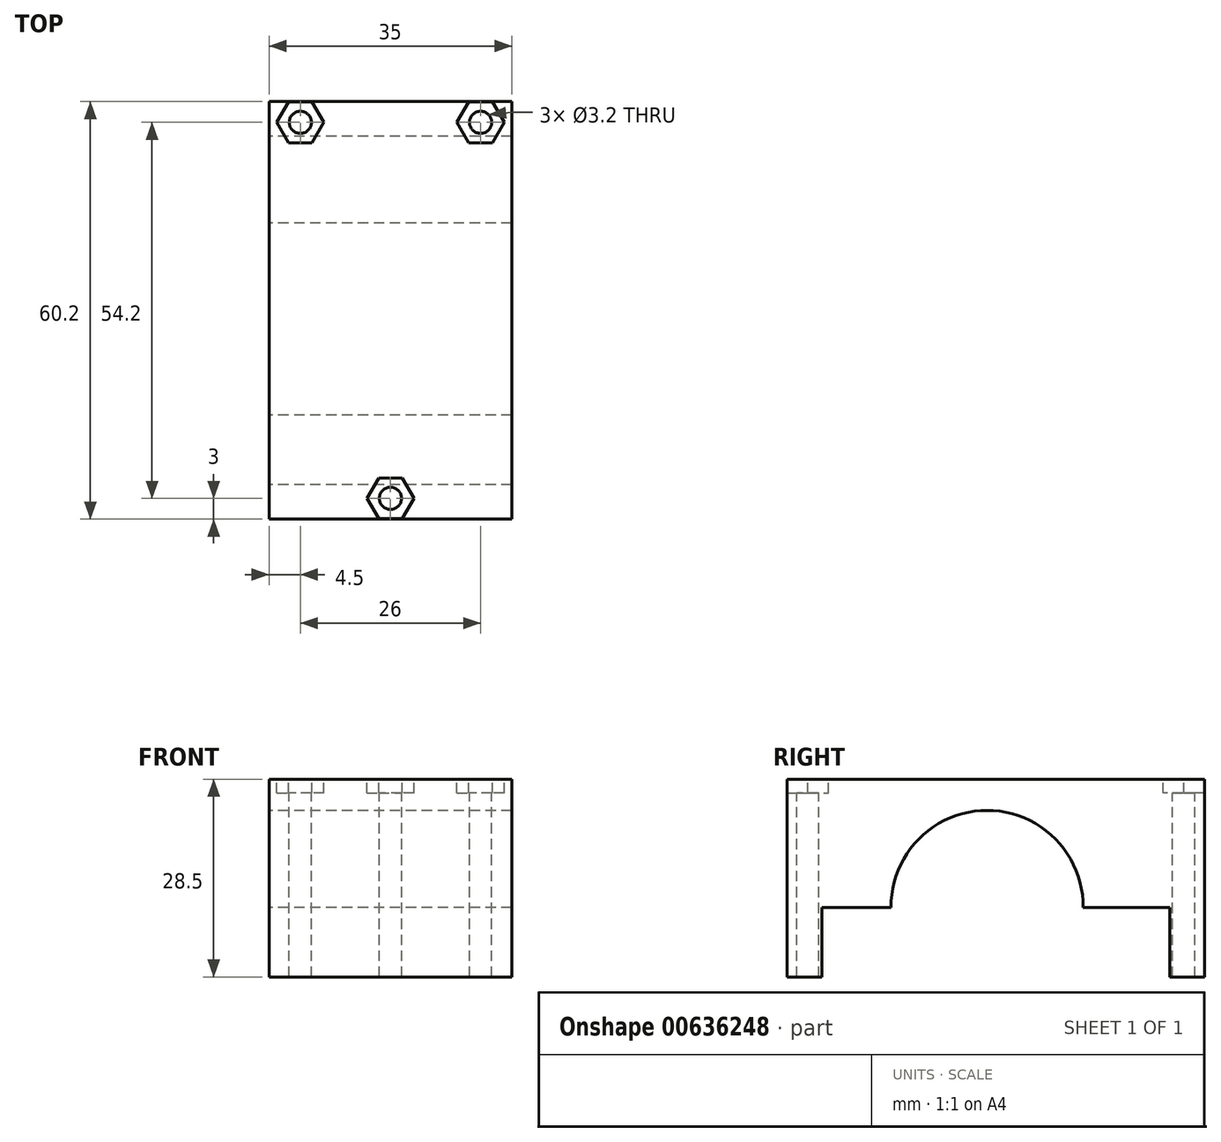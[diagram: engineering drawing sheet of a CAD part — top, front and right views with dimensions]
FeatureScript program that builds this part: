
annotation { "Feature Type Name" : "Feature", "Feature Type Description" : "" }
export const myFeature = defineFeature(function(context is Context, id is Id, definition is map)
    precondition{}
    {
        {
            var Q0;
            Q0=qCreatedBy(makeId("Right.planeOp"),FACE);
            var sketch = newSketch(context, id + "F0", { "sketchPlane" : qUnion([Q0])});
            skLineSegment(sketch, "E0.top", {"start": v(0, 28.5) * mm, "end": v(-60.2, 28.5) * mm});
            skLineSegment(sketch, "E0.left", {"start": v(0, 0) * mm, "end": v(0, 28.5) * mm});
            skLineSegment(sketch, "E0.right", {"start": v(-60.2, 0) * mm, "end": v(-60.2, 28.5) * mm});
            skLineSegment(sketch, "E1", {"start": v(-60.2, 0) * mm, "end": v(-55.2, 0) * mm});
            skLineSegment(sketch, "E2", {"start": v(0, 0) * mm, "end": v(-5, 0) * mm});
            skLineSegment(sketch, "E3", {"start": v(-55.2, 0) * mm, "end": v(-55.2, 10) * mm});
            skLineSegment(sketch, "E4", {"start": v(-5, 0) * mm, "end": v(-5, 10) * mm});
            skLineSegment(sketch, "E5", {"start": v(-55.2, 10) * mm, "end": v(-45.2, 10) * mm});
            skLineSegment(sketch, "E6", {"start": v(-5, 10) * mm, "end": v(-17.5, 10) * mm});
            skArc(sketch, "E7", {"start": v(-17.5, 10) * mm, "mid": v(-31.35, 24) * mm, "end": v(-45.2, 10) * mm});
            skPoint(sketch, "E8", {"position": v(-31.35, 24) * mm});
            skSolve(sketch);
        }
        {
            var Q0;
            Q0 = qSketchRegion(id + "F0", true);
            extrude(context, id + "F1", {"entities" : qUnion([Q0]), "depth" : 35 * mm, "offsetDistance" : 25 * mm});
        }
        {
            var Q0;
            Q0=makeQuery(id+"F1.opExtrude","SWEPT_FACE",FACE,{"disambiguationData":[OSD([sQuery(id+"F0.wireOp",EDGE,"E0.top")])]});
            var sketch = newSketch(context, id + "F2", { "sketchPlane" : qUnion([Q0])});
            skCircle(sketch, "E9", {"center": v(4.5, -3) * mm, "radius": 1.6 * mm});
            skCircle(sketch, "E10", {"center": v(30.5, -3) * mm, "radius": 1.6 * mm});
            skCircle(sketch, "E11", {"center": v(17.5, -57.2) * mm, "radius": 1.6 * mm});
            skSolve(sketch);
        }
        {
            var Q0;
            Q0 = qSketchRegion(id + "F2", true);
            extrude(context, id + "F3", {"entities" : qUnion([Q0]), "operationType" : NewBodyOperationType.REMOVE, "endBound" : BoundingType.UP_TO_NEXT, "oppositeDirection" : true, "depth" : 25 * mm, "offsetDistance" : 25 * mm});
        }
        {
            var Q0;
            Q0=makeQuery(id+"F1.opExtrude","SWEPT_FACE",FACE,{"disambiguationData":[OSD([sQuery(id+"F0.wireOp",EDGE,"E0.top")])]});
            var sketch = newSketch(context, id + "F4", { "sketchPlane" : qUnion([Q0])});
            skCircle(sketch, "E12.cCircle", {"center": v(4.5, -3) * mm, "radius": 2.95 * mm, "construction": true});
            skLineSegment(sketch, "E12.0", {"start": v(6.2, -5.95) * mm, "end": v(2.8, -5.95) * mm});
            skLineSegment(sketch, "E12.1", {"start": v(2.8, -5.95) * mm, "end": v(1.1, -3) * mm});
            skLineSegment(sketch, "E12.2", {"start": v(1.1, -3) * mm, "end": v(2.8, -0.05) * mm});
            skLineSegment(sketch, "E12.3", {"start": v(2.8, -0.05) * mm, "end": v(6.2, -0.05) * mm});
            skLineSegment(sketch, "E12.4", {"start": v(6.2, -0.05) * mm, "end": v(7.9, -3) * mm});
            skLineSegment(sketch, "E12.5", {"start": v(7.9, -3) * mm, "end": v(6.2, -5.95) * mm});
            skPoint(sketch, "E12.0.midPoint", {"position": v(4.5, -5.95) * mm});
            skCircle(sketch, "E13.cCircle", {"center": v(30.5, -3) * mm, "radius": 2.95 * mm, "construction": true});
            skLineSegment(sketch, "E13.0", {"start": v(32.2, -5.95) * mm, "end": v(28.8, -5.95) * mm});
            skLineSegment(sketch, "E13.1", {"start": v(28.8, -5.95) * mm, "end": v(27.1, -3) * mm});
            skLineSegment(sketch, "E13.2", {"start": v(27.1, -3) * mm, "end": v(28.8, -0.05) * mm});
            skLineSegment(sketch, "E13.3", {"start": v(28.8, -0.05) * mm, "end": v(32.2, -0.05) * mm});
            skLineSegment(sketch, "E13.4", {"start": v(32.2, -0.05) * mm, "end": v(33.9, -3) * mm});
            skLineSegment(sketch, "E13.5", {"start": v(33.9, -3) * mm, "end": v(32.2, -5.95) * mm});
            skPoint(sketch, "E13.0.midPoint", {"position": v(30.5, -5.95) * mm});
            skPoint(sketch, "E14.0.midPoint", {"position": v(17.5, -60.15) * mm});
            skCircle(sketch, "E15.cCircle", {"center": v(17.5, -57.2) * mm, "radius": 2.95 * mm, "construction": true});
            skLineSegment(sketch, "E15.0", {"start": v(15.8, -54.25) * mm, "end": v(19.2, -54.25) * mm});
            skLineSegment(sketch, "E15.1", {"start": v(19.2, -54.25) * mm, "end": v(20.9, -57.2) * mm});
            skLineSegment(sketch, "E15.2", {"start": v(20.9, -57.2) * mm, "end": v(19.2, -60.15) * mm});
            skLineSegment(sketch, "E15.3", {"start": v(19.2, -60.15) * mm, "end": v(15.8, -60.15) * mm});
            skLineSegment(sketch, "E15.4", {"start": v(15.8, -60.15) * mm, "end": v(14.1, -57.2) * mm});
            skLineSegment(sketch, "E15.5", {"start": v(14.1, -57.2) * mm, "end": v(15.8, -54.25) * mm});
            skPoint(sketch, "E15.0.midPoint", {"position": v(17.5, -54.25) * mm});
            skSolve(sketch);
        }
        {
            var Q0;
            Q0 = qSketchRegion(id + "F4", true);
            extrude(context, id + "F5", {"entities" : qUnion([Q0]), "operationType" : NewBodyOperationType.REMOVE, "oppositeDirection" : true, "depth" : 2 * mm, "offsetDistance" : 25 * mm});
        }
    });
